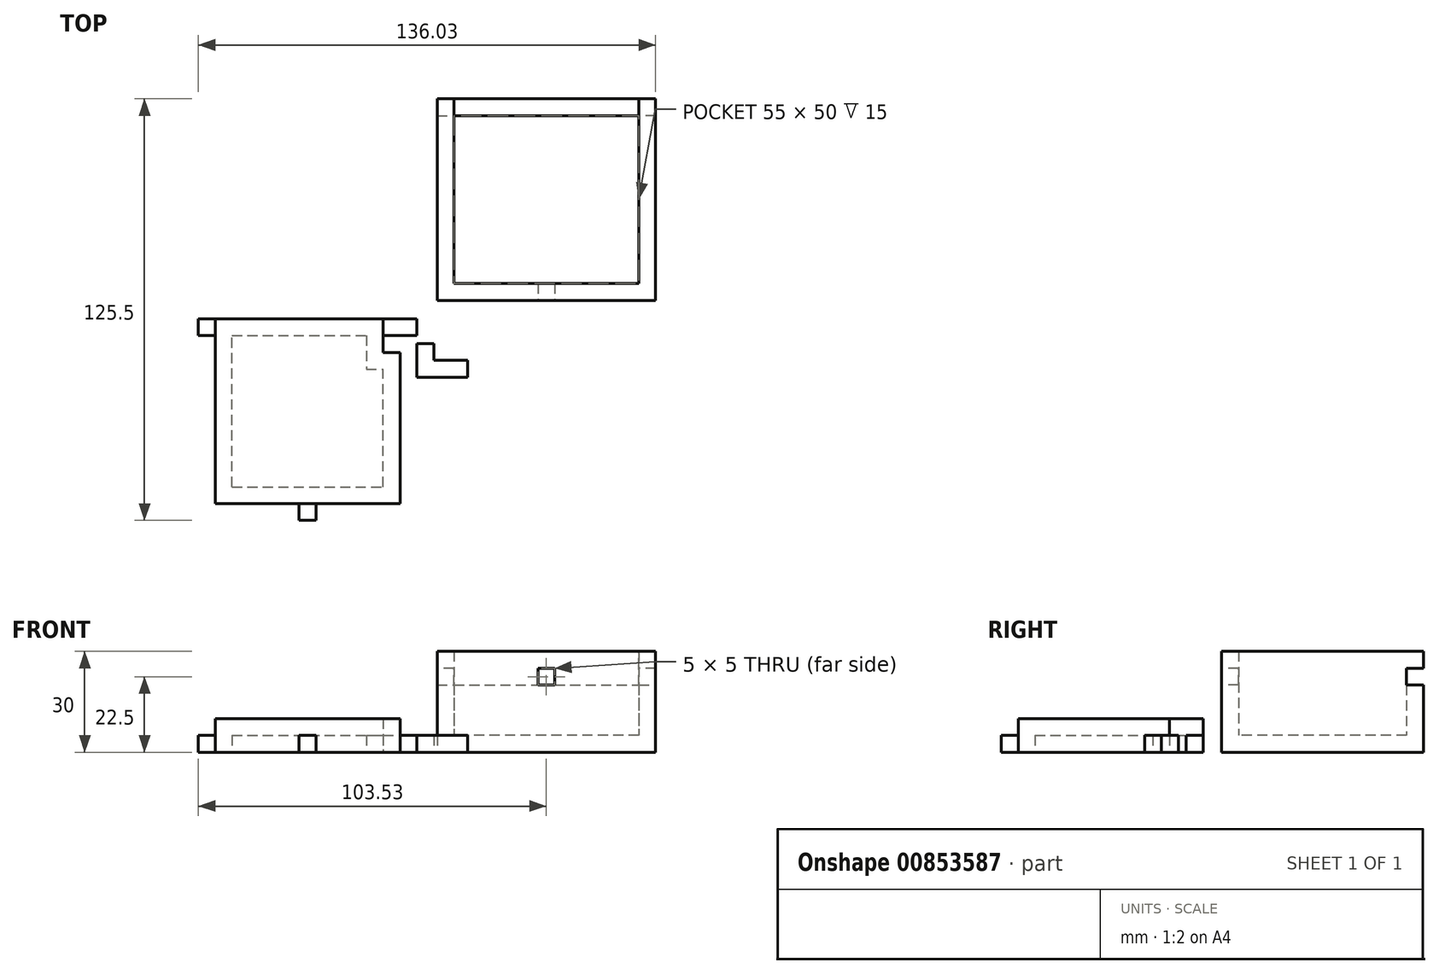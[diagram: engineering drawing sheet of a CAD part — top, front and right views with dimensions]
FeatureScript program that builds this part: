
annotation { "Feature Type Name" : "Feature", "Feature Type Description" : "" }
export const myFeature = defineFeature(function(context is Context, id is Id, definition is map)
    precondition{}
    {
        {
            assignVariable(context, id + "F0", {"name" : "T", "anyValue" : 5});
        }
        {
            assignVariable(context, id + "F1", {"name" : "H", "anyValue" : 30});
        }
        {
            assignVariable(context, id + "F2", {"name" : "LU", "anyValue" : 5});
        }
        {
            assignVariable(context, id + "F3", {"name" : "LL", "anyValue" : 5});
        }
        {
            assignVariable(context, id + "F4", {"name" : "KW", "anyValue" : 5});
        }
        {
            var Q0;
            Q0=qCreatedBy(makeId("Top.planeOp"),FACE);
            var sketch = newSketch(context, id + "F5", { "sketchPlane" : qUnion([Q0])});
            skLineSegment(sketch, "E0.bottom", {"start": v(0, 0) * mm, "end": v(65, 0) * mm});
            skLineSegment(sketch, "E0.top", {"start": v(0, 60) * mm, "end": v(65, 60) * mm});
            skLineSegment(sketch, "E0.left", {"start": v(0, 0) * mm, "end": v(0, 60) * mm});
            skLineSegment(sketch, "E0.right", {"start": v(65, 0) * mm, "end": v(65, 60) * mm});
            skLineSegment(sketch, "E1.bottom", {"start": v(60, 55) * mm, "end": v(5, 55) * mm});
            skLineSegment(sketch, "E1.top", {"start": v(60, 5) * mm, "end": v(5, 5) * mm});
            skLineSegment(sketch, "E1.left", {"start": v(60, 55) * mm, "end": v(60, 5) * mm});
            skLineSegment(sketch, "E1.right", {"start": v(5, 55) * mm, "end": v(5, 5) * mm});
            skLineSegment(sketch, "E2.bottom", {"start": v(-66.03, -5.5) * mm, "end": v(-16.03, -5.5) * mm});
            skLineSegment(sketch, "E2.top", {"start": v(-66.03, -60.5) * mm, "end": v(-11.03, -60.5) * mm});
            skLineSegment(sketch, "E2.left", {"start": v(-66.03, -5.5) * mm, "end": v(-66.03, -60.5) * mm});
            skLineSegment(sketch, "E3.bottom", {"start": v(-66.03, -5.5) * mm, "end": v(-71.03, -5.5) * mm});
            skLineSegment(sketch, "E3.top", {"start": v(-66.03, -10.5) * mm, "end": v(-71.03, -10.5) * mm});
            skLineSegment(sketch, "E3.left", {"start": v(-66.03, -5.5) * mm, "end": v(-66.03, -10.5) * mm});
            skLineSegment(sketch, "E3.right", {"start": v(-71.03, -5.5) * mm, "end": v(-71.03, -10.5) * mm});
            skLineSegment(sketch, "E4.bottom", {"start": v(-41.03, -60.5) * mm, "end": v(-36.03, -60.5) * mm});
            skLineSegment(sketch, "E4.top", {"start": v(-41.03, -65.5) * mm, "end": v(-36.03, -65.5) * mm});
            skLineSegment(sketch, "E4.left", {"start": v(-41.03, -60.5) * mm, "end": v(-41.03, -65.5) * mm});
            skLineSegment(sketch, "E4.right", {"start": v(-36.03, -60.5) * mm, "end": v(-36.03, -65.5) * mm});
            skLineSegment(sketch, "E5.bottom", {"start": v(-16.03, -5.5) * mm, "end": v(-6.03, -5.5) * mm});
            skLineSegment(sketch, "E5.top", {"start": v(-16.03, -10.5) * mm, "end": v(-6.03, -10.5) * mm});
            skLineSegment(sketch, "E5.left", {"start": v(-16.03, -5.5) * mm, "end": v(-16.03, -10.5) * mm});
            skLineSegment(sketch, "E5.right", {"start": v(-6.03, -5.5) * mm, "end": v(-6.03, -10.5) * mm});
            skLineSegment(sketch, "E6", {"start": v(-16.03, -10.5) * mm, "end": v(-16.03, -15.5) * mm});
            skLineSegment(sketch, "E7", {"start": v(-16.03, -15.5) * mm, "end": v(-11.03, -15.5) * mm});
            skLineSegment(sketch, "E8", {"start": v(-11.03, -15.5) * mm, "end": v(-11.03, -60.5) * mm});
            skLineSegment(sketch, "E9.top", {"start": v(-5.99, -22.9) * mm, "end": v(9.01, -22.9) * mm});
            skLineSegment(sketch, "E9.left", {"start": v(-5.99, -12.9) * mm, "end": v(-5.99, -22.9) * mm});
            skLineSegment(sketch, "E9.right", {"start": v(9.01, -17.9) * mm, "end": v(9.01, -22.9) * mm});
            skLineSegment(sketch, "E10.top", {"start": v(-0.99, -17.9) * mm, "end": v(9.01, -17.9) * mm});
            skLineSegment(sketch, "E10.right", {"start": v(-0.99, -12.9) * mm, "end": v(-0.99, -17.9) * mm});
            skLineSegment(sketch, "E11", {"start": v(-5.99, -12.9) * mm, "end": v(-0.99, -12.9) * mm});
            skLineSegment(sketch, "E12.top", {"start": v(-61.03, -10.5) * mm, "end": v(-21.03, -10.5) * mm});
            skLineSegment(sketch, "E12.left", {"start": v(-61.03, -55.5) * mm, "end": v(-61.03, -10.5) * mm});
            skLineSegment(sketch, "E13.top", {"start": v(-21.03, -20.5) * mm, "end": v(-16.03, -20.5) * mm});
            skLineSegment(sketch, "E13.right", {"start": v(-16.03, -55.5) * mm, "end": v(-16.03, -20.5) * mm});
            skLineSegment(sketch, "E14", {"start": v(-21.03, -10.5) * mm, "end": v(-21.03, -20.5) * mm});
            skLineSegment(sketch, "E15", {"start": v(-61.03, -55.5) * mm, "end": v(-16.03, -55.5) * mm});
            skSolve(sketch);
        }
        {
            var Q0;
            Q0=makeQuery(id+"F5.imprint","IMPRINT",FACE,{"disambiguationData":[TD([[makeQuery(id+"F5.imprint","IMPRINT",EDGE,{"derivedFrom":sQuery(id+"F5.wireOp",EDGE,"E1.bottom")}),1.0]])]});
            extrude(context, id + "F6", {"entities" : qUnion([Q0]), "depth" : (getVariable(context, 'T')) * mm, "offsetDistance" : 25 * mm});
        }
        {
            var Q0;
            Q0=makeQuery(id+"F5.imprint","IMPRINT",FACE,{"disambiguationData":[TD([[makeQuery(id+"F5.imprint","IMPRINT",EDGE,{"derivedFrom":sQuery(id+"F5.wireOp",EDGE,"E0.bottom")}),1.0]])]});
            extrude(context, id + "F7", {"entities" : qUnion([Q0]), "operationType" : NewBodyOperationType.ADD, "depth" : (getVariable(context, 'H')) * mm, "offsetDistance" : 25 * mm});
        }
        {
            var Q0;
            Q0=makeQuery(id+"F7.opExtrude","SWEPT_FACE",FACE,{"disambiguationData":[OSD([sQuery(id+"F5.wireOp",EDGE,"E0.top")])]});
            var sketch = newSketch(context, id + "F8", { "sketchPlane" : qUnion([Q0])});
            skLineSegment(sketch, "E16", {"start": v(-65, 25) * mm, "end": v(-60, 25) * mm});
            skLineSegment(sketch, "E17", {"start": v(-60, 25) * mm, "end": v(-60, 30) * mm});
            skLineSegment(sketch, "E18", {"start": v(-60, 30) * mm, "end": v(-5, 30) * mm});
            skLineSegment(sketch, "E19", {"start": v(-5, 30) * mm, "end": v(-5, 25) * mm});
            skLineSegment(sketch, "E20", {"start": v(-5, 25) * mm, "end": v(0, 25) * mm});
            skLineSegment(sketch, "E21", {"start": v(0, 25) * mm, "end": v(0, 20) * mm});
            skLineSegment(sketch, "E22", {"start": v(0, 20) * mm, "end": v(-65, 20) * mm});
            skLineSegment(sketch, "E23", {"start": v(-65, 20) * mm, "end": v(-65, 25) * mm});
            skSolve(sketch);
        }
        {
            var Q0;
            Q0=makeQuery(id+"F8.imprint","IMPRINT",FACE,{"disambiguationData":[TD([[makeQuery(id+"F8.imprint","IMPRINT",EDGE,{"derivedFrom":sQuery(id+"F8.wireOp",EDGE,"E16")}),-1.0]])]});
            extrude(context, id + "F9", {"entities" : qUnion([Q0]), "operationType" : NewBodyOperationType.REMOVE, "oppositeDirection" : true, "depth" : (getVariable(context, 'T')) * mm, "offsetDistance" : 25 * mm});
        }
        {
            var Q0;
            {var subQ2=sQuery(id+"F5.wireOp",EDGE,"E2.bottom");Q0=makeQuery(id+"F5.imprint","IMPRINT",FACE,{"disambiguationData":[TD([[makeQuery(id+"F5.imprint","IMPRINT",EDGE,{"derivedFrom":subQ2}),-1.0]])]});}
            var Q1;
            Q1=makeQuery(id+"F5.imprint","IMPRINT",FACE,{"disambiguationData":[TD([[makeQuery(id+"F5.imprint","IMPRINT",EDGE,{"derivedFrom":sQuery(id+"F5.wireOp",EDGE,"E12.top")}),-1.0]])]});
            extrude(context, id + "F10", {"entities" : qUnion([Q0, Q1]), "depth" : (getVariable(context, 'LL') + getVariable(context, 'LU')) * mm, "offsetDistance" : 25 * mm});
        }
        {
            var Q0;
            Q0=makeQuery(id+"F5.imprint","IMPRINT",FACE,{"disambiguationData":[TD([[makeQuery(id+"F5.imprint","IMPRINT",EDGE,{"derivedFrom":sQuery(id+"F5.wireOp",EDGE,"E12.top")}),-1.0]])]});
            extrude(context, id + "F11", {"entities" : qUnion([Q0]), "operationType" : NewBodyOperationType.REMOVE, "depth" : (getVariable(context, 'LL')) * mm, "offsetDistance" : 25 * mm});
        }
        {
            var Q0;
            Q0=makeQuery(id+"F5.imprint","IMPRINT",FACE,{"disambiguationData":[TD([[makeQuery(id+"F5.imprint","IMPRINT",EDGE,{"derivedFrom":sQuery(id+"F5.wireOp",EDGE,"E5.bottom")}),-1.0]])]});
            var Q1;
            Q1=makeQuery(id+"F5.imprint","IMPRINT",FACE,{"disambiguationData":[TD([[makeQuery(id+"F5.imprint","IMPRINT",EDGE,{"derivedFrom":sQuery(id+"F5.wireOp",EDGE,"E4.top")}),1.0]])]});
            var Q2;
            {var subQ0=sQuery(id+"F5.wireOp",EDGE,"E3.bottom");Q2=makeQuery(id+"F5.imprint","IMPRINT",FACE,{"disambiguationData":[TD([[makeQuery(id+"F5.imprint","IMPRINT",EDGE,{"derivedFrom":subQ0}),1.0]])]});}
            extrude(context, id + "F12", {"entities" : qUnion([Q0, Q1, Q2]), "operationType" : NewBodyOperationType.ADD, "depth" : (getVariable(context, 'LL')) * mm, "offsetDistance" : 25 * mm});
        }
        {
            var Q0;
            Q0=makeQuery(id+"F7.opExtrude","SWEPT_FACE",FACE,{"disambiguationData":[OSD([sQuery(id+"F5.wireOp",EDGE,"E0.bottom")])]});
            var sketch = newSketch(context, id + "F13", { "sketchPlane" : qUnion([Q0])});
            skLineSegment(sketch, "E24.bottom", {"start": v(30, 25) * mm, "end": v(35, 25) * mm});
            skLineSegment(sketch, "E24.top", {"start": v(30, 20) * mm, "end": v(35, 20) * mm});
            skLineSegment(sketch, "E24.left", {"start": v(30, 25) * mm, "end": v(30, 20) * mm});
            skLineSegment(sketch, "E24.right", {"start": v(35, 25) * mm, "end": v(35, 20) * mm});
            skSolve(sketch);
        }
        {
            var Q0;
            Q0=makeQuery(id+"F13.imprint","IMPRINT",FACE,{"disambiguationData":[TD([[makeQuery(id+"F13.imprint","IMPRINT",EDGE,{"derivedFrom":sQuery(id+"F13.wireOp",EDGE,"E24.bottom")}),-1.0]])]});
            var Q1;
            Q1=makeQuery(id+"F7.opExtrude","SWEPT_FACE",FACE,{"disambiguationData":[OSD([sQuery(id+"F5.wireOp",EDGE,"E1.top")])]});
            extrude(context, id + "F14", {"entities" : qUnion([Q0]), "operationType" : NewBodyOperationType.REMOVE, "endBound" : BoundingType.UP_TO_SURFACE, "oppositeDirection" : true, "depth" : (getVariable(context, 'T')) * mm, "endBoundEntityFace" : qUnion([Q1]), "offsetDistance" : 25 * mm});
        }
        {
            var Q0;
            Q0=makeQuery(id+"F5.imprint","IMPRINT",FACE,{"disambiguationData":[TD([[makeQuery(id+"F5.imprint","IMPRINT",EDGE,{"derivedFrom":sQuery(id+"F5.wireOp",EDGE,"E9.top")}),1.0]])]});
            extrude(context, id + "F15", {"entities" : qUnion([Q0]), "depth" : (getVariable(context, 'KW')) * mm, "offsetDistance" : 25 * mm});
        }
    });
